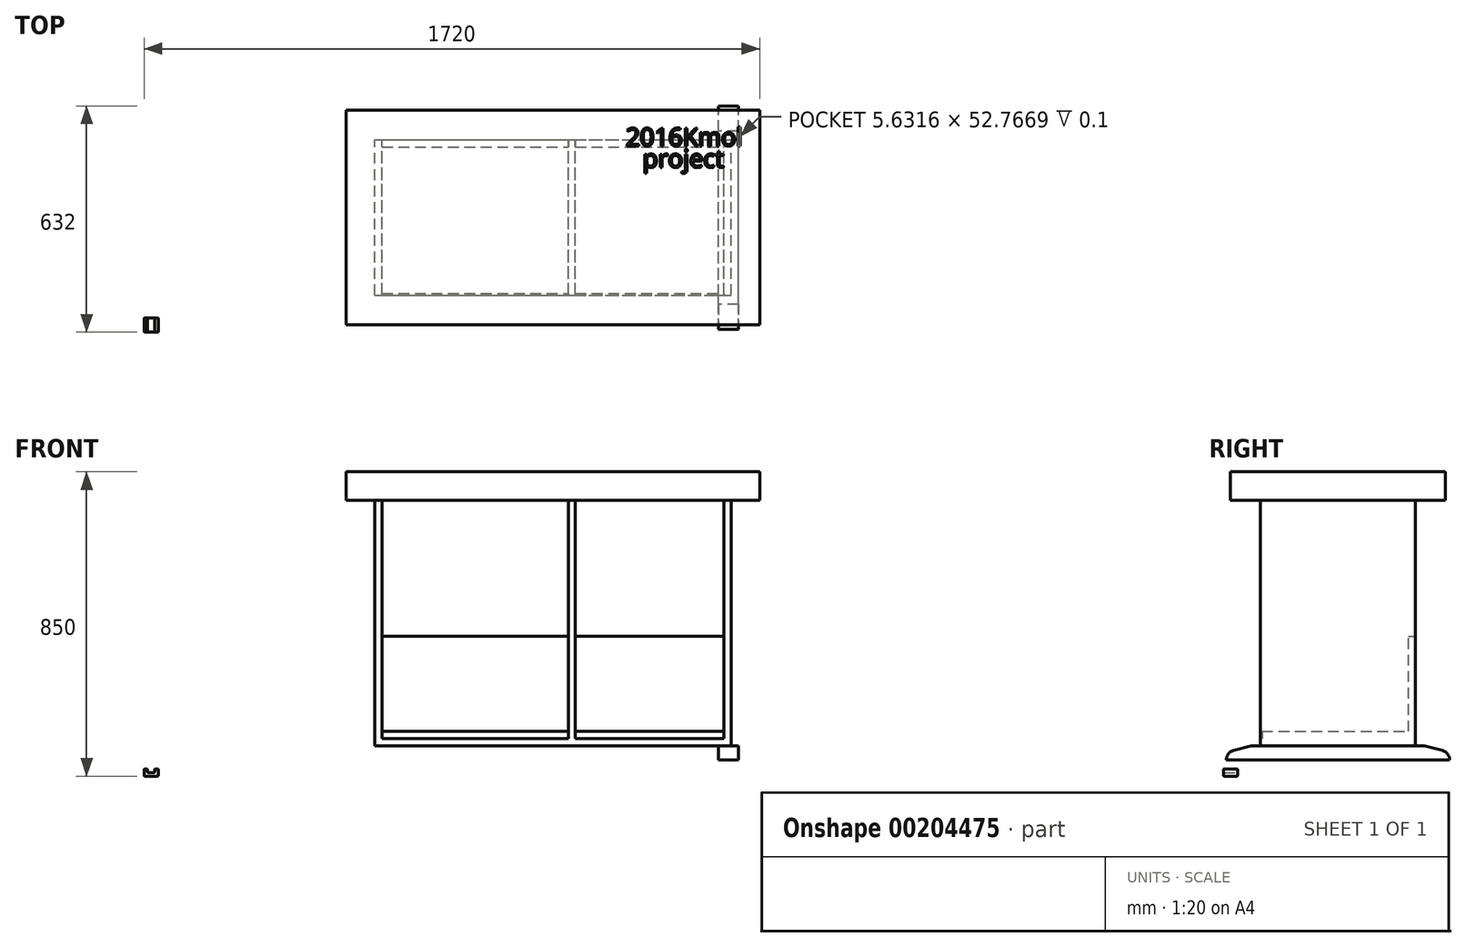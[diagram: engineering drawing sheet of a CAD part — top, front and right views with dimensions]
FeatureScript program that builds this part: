
annotation { "Feature Type Name" : "Feature", "Feature Type Description" : "" }
export const myFeature = defineFeature(function(context is Context, id is Id, definition is map)
    precondition{}
    {
        {
            var Q0;
            Q0=qCreatedBy(makeId("Top.planeOp"),FACE);
            cPlane(context, id + "F0", {"entities" : qUnion([Q0]), "cplaneType" : CPlaneType.OFFSET, "offset" : 770 * mm, "width" : 150 * mm, "height" : 150 * mm});
        }
        {
            var Q0;
            Q0=qCreatedBy(id+"F0.planeOp",FACE);
            var sketch = newSketch(context, id + "F1", { "sketchPlane" : qUnion([Q0])});
            skLineSegment(sketch, "E0.bottom", {"start": v(545, 0) * mm, "end": v(1700, 0) * mm});
            skLineSegment(sketch, "E0.top", {"start": v(545, 600) * mm, "end": v(1700, 600) * mm});
            skLineSegment(sketch, "E0.left", {"start": v(545, 0) * mm, "end": v(545, 600) * mm});
            skLineSegment(sketch, "E0.right", {"start": v(1700, 0) * mm, "end": v(1700, 600) * mm});
            skSolve(sketch);
        }
        {
            var Q0;
            Q0=makeQuery(id+"F1.imprint","IMPRINT",FACE,{"disambiguationData":[TD([[makeQuery(id+"F1.imprint","IMPRINT",EDGE,{"derivedFrom":sQuery(id+"F1.wireOp",EDGE,"E0.bottom")}),1.0]])]});
            extrude(context, id + "F2", {"entities" : qUnion([Q0]), "depth" : 80 * mm});
        }
        {
            var Q0;
            Q0=makeQuery(id+"F2.opExtrude","CAP_FACE",FACE,{"disambiguationData":[OSD([sQuery(id+"F1.wireOp",EDGE,"E0.bottom"),sQuery(id+"F1.wireOp",EDGE,"E0.top"),sQuery(id+"F1.wireOp",EDGE,"E0.left"),sQuery(id+"F1.wireOp",EDGE,"E0.right")])],"isStart":true});
            var sketch = newSketch(context, id + "F3", { "sketchPlane" : qUnion([Q0])});
            skLineSegment(sketch, "E1.bottom", {"start": v(1600, -83) * mm, "end": v(1620, -83) * mm});
            skLineSegment(sketch, "E1.top", {"start": v(1600, -517) * mm, "end": v(1620, -517) * mm});
            skLineSegment(sketch, "E1.left", {"start": v(1600, -83) * mm, "end": v(1600, -517) * mm});
            skLineSegment(sketch, "E1.right", {"start": v(1620, -83) * mm, "end": v(1620, -517) * mm});
            skLineSegment(sketch, "E2.bottom", {"start": v(1165, -83) * mm, "end": v(1185, -83) * mm});
            skLineSegment(sketch, "E2.top", {"start": v(1165, -517) * mm, "end": v(1185, -517) * mm});
            skLineSegment(sketch, "E2.left", {"start": v(1185, -83) * mm, "end": v(1185, -517) * mm});
            skLineSegment(sketch, "E2.right", {"start": v(1165, -83) * mm, "end": v(1165, -517) * mm});
            skLineSegment(sketch, "E3.bottom", {"start": v(625, -83) * mm, "end": v(645, -83) * mm});
            skLineSegment(sketch, "E3.top", {"start": v(625, -517) * mm, "end": v(645, -517) * mm});
            skLineSegment(sketch, "E3.left", {"start": v(625, -83) * mm, "end": v(625, -517) * mm});
            skLineSegment(sketch, "E3.right", {"start": v(645, -83) * mm, "end": v(645, -517) * mm});
            skSolve(sketch);
        }
        {
            var Q0;
            Q0=qSketchRegion(id+"F3",true);
            extrude(context, id + "F4", {"entities" : qUnion([Q0]), "operationType" : NewBodyOperationType.ADD, "depth" : 685 * mm});
        }
        {
            var Q0;
            Q0=makeQuery(id+"F4.opExtrude","CAP_FACE",FACE,{"disambiguationData":[OSD([sQuery(id+"F3.wireOp",EDGE,"E3.bottom"),sQuery(id+"F3.wireOp",EDGE,"E3.top"),sQuery(id+"F3.wireOp",EDGE,"E3.left"),sQuery(id+"F3.wireOp",EDGE,"E3.right")])],"isStart":false});
            var sketch = newSketch(context, id + "F5", { "sketchPlane" : qUnion([Q0])});
            skLineSegment(sketch, "E4.bottom", {"start": v(625, -517) * mm, "end": v(1620, -517) * mm});
            skLineSegment(sketch, "E4.top", {"start": v(625, -83) * mm, "end": v(1620, -83) * mm});
            skLineSegment(sketch, "E4.left", {"start": v(625, -517) * mm, "end": v(625, -83) * mm});
            skLineSegment(sketch, "E4.right", {"start": v(1620, -517) * mm, "end": v(1620, -83) * mm});
            skSolve(sketch);
        }
        {
            var Q0;
            {var subQ2=sQuery(id+"F5.wireOp",EDGE,"E4.right");Q0=makeQuery(id+"F5.imprint","IMPRINT",FACE,{"disambiguationData":[TD([[makeQuery(id+"F5.imprint","IMPRINT",EDGE,{"derivedFrom":subQ2}),1.0]])]});}
            extrude(context, id + "F6", {"entities" : qUnion([Q0]), "operationType" : NewBodyOperationType.ADD, "oppositeDirection" : true, "depth" : 40 * mm});
        }
        {
            var Q0;
            Q0=makeQuery(id+"F6.boolean.opBoolean","MERGE",FACE,{"derivedFrom":[makeQuery(id+"F4.opExtrude","SWEPT_FACE",FACE,{"disambiguationData":[OSD([sQuery(id+"F3.wireOp",EDGE,"E1.bottom")])]}),makeQuery(id+"F4.opExtrude","SWEPT_FACE",FACE,{"disambiguationData":[OSD([sQuery(id+"F3.wireOp",EDGE,"E2.bottom")])]}),makeQuery(id+"F4.opExtrude","SWEPT_FACE",FACE,{"disambiguationData":[OSD([sQuery(id+"F3.wireOp",EDGE,"E3.bottom")])]}),makeQuery(id+"F6.opExtrude","SWEPT_FACE",FACE,{"disambiguationData":[OSD([sQuery(id+"F5.wireOp",EDGE,"E4.top")])]})]});
            var sketch = newSketch(context, id + "F7", { "sketchPlane" : qUnion([Q0])});
            skLineSegment(sketch, "E5.bottom", {"start": v(645, 125) * mm, "end": v(1165, 125) * mm});
            skLineSegment(sketch, "E5.top", {"start": v(645, 105) * mm, "end": v(1165, 105) * mm});
            skLineSegment(sketch, "E5.left", {"start": v(645, 125) * mm, "end": v(645, 105) * mm});
            skLineSegment(sketch, "E5.right", {"start": v(1165, 125) * mm, "end": v(1165, 105) * mm});
            skLineSegment(sketch, "E6.bottom", {"start": v(1185, 125) * mm, "end": v(1600, 125) * mm});
            skLineSegment(sketch, "E6.top", {"start": v(1185, 105) * mm, "end": v(1600, 105) * mm});
            skLineSegment(sketch, "E6.left", {"start": v(1185, 125) * mm, "end": v(1185, 105) * mm});
            skLineSegment(sketch, "E6.right", {"start": v(1600, 125) * mm, "end": v(1600, 105) * mm});
            skSolve(sketch);
        }
        {
            var Q0;
            Q0=qSketchRegion(id+"F7",true);
            extrude(context, id + "F8", {"entities" : qUnion([Q0]), "operationType" : NewBodyOperationType.REMOVE, "oppositeDirection" : true, "depth" : 5 * mm});
        }
        {
            var Q0;
            Q0=makeQuery(id+"F8.boolean.opBoolean","MERGE",FACE,{"derivedFrom":[makeQuery(id+"F4.opExtrude","SWEPT_FACE",FACE,{"disambiguationData":[OSD([sQuery(id+"F3.wireOp",EDGE,"E1.left")])]}),makeQuery(id+"F8.opExtrude","SWEPT_FACE",FACE,{"disambiguationData":[OSD([sQuery(id+"F7.wireOp",EDGE,"E6.right")])]})]});
            var sketch = newSketch(context, id + "F9", { "sketchPlane" : qUnion([Q0])});
            skLineSegment(sketch, "E7.bottom", {"start": v(-517, 390) * mm, "end": v(-497, 390) * mm});
            skLineSegment(sketch, "E7.top", {"start": v(-517, 125) * mm, "end": v(-497, 125) * mm});
            skLineSegment(sketch, "E7.left", {"start": v(-517, 390) * mm, "end": v(-517, 125) * mm});
            skLineSegment(sketch, "E7.right", {"start": v(-497, 390) * mm, "end": v(-497, 125) * mm});
            skSolve(sketch);
        }
        {
            var Q0;
            Q0=qSketchRegion(id+"F9",true);
            var Q1;
            Q1=makeQuery(id+"F8.boolean.opBoolean","MERGE",FACE,{"derivedFrom":[makeQuery(id+"F4.opExtrude","SWEPT_FACE",FACE,{"disambiguationData":[OSD([sQuery(id+"F3.wireOp",EDGE,"E3.right")])]}),makeQuery(id+"F8.opExtrude","SWEPT_FACE",FACE,{"disambiguationData":[OSD([sQuery(id+"F7.wireOp",EDGE,"E5.left")])]})]});
            extrude(context, id + "F10", {"entities" : qUnion([Q0]), "operationType" : NewBodyOperationType.ADD, "endBound" : BoundingType.UP_TO_SURFACE, "endBoundEntityFace" : qUnion([Q1]), "depth" : 25 * mm});
        }
        {
            var Q0;
            Q0=makeQuery(id+"F2.opExtrude","CAP_FACE",FACE,{"disambiguationData":[OSD([sQuery(id+"F1.wireOp",EDGE,"E0.bottom"),sQuery(id+"F1.wireOp",EDGE,"E0.top"),sQuery(id+"F1.wireOp",EDGE,"E0.left"),sQuery(id+"F1.wireOp",EDGE,"E0.right")])],"isStart":false});
            var sketch = newSketch(context, id + "F11", { "sketchPlane" : qUnion([Q0])});
            skText(sketch, "E8", { "text": "2016Kmol", "fontName": "OpenSans-Regular.ttf"});
            skText(sketch, "E9", { "text": "project", "fontName": "OpenSans-Regular.ttf"});
            const initialGuessF11  = {"E8": [1.32592, 0.5, 1, 0, 0.05], "E9": [1.37295, 0.44, 1, 0, 0.05]};
            skSetInitialGuess(sketch, initialGuessF11);
            skSolve(sketch);
        }
        {
            var Q0;
            Q0=qSketchRegion(id+"F11",true);
            extrude(context, id + "F12", {"entities" : qUnion([Q0]), "operationType" : NewBodyOperationType.REMOVE, "oppositeDirection" : true, "depth" : 0.1 * mm});
        }
        {
            var Q0;
            Q0=makeQuery(id+"F4.opExtrude","SWEPT_FACE",FACE,{"disambiguationData":[OSD([sQuery(id+"F3.wireOp",EDGE,"E1.right")])]});
            var sketch = newSketch(context, id + "F13", { "sketchPlane" : qUnion([Q0])});
            skLineSegment(sketch, "E10", {"start": v(58, 85) * mm, "end": v(8, 71.24) * mm});
            skArc(sketch, "E11", {"start": v(8, 71.24) * mm, "mid": v(-6.43, 61.5) * mm, "end": v(-12, 45) * mm});
            skLineSegment(sketch, "E12", {"start": v(-12, 45) * mm, "end": v(300, 45) * mm});
            skPoint(sketch, "E12.endSnap0", {"position": v(300, 85) * mm});
            skLineSegment(sketch, "E13", {"start": v(58, 85) * mm, "end": v(300, 85) * mm});
            skLineSegment(sketch, "E14", {"start": v(300, 85) * mm, "end": v(300, -33.8) * mm, "construction": true});
            skLineSegment(sketch, "E15.MirrorCS", {"start": v(542, 85) * mm, "end": v(300, 85) * mm});
            skLineSegment(sketch, "E16.MirrorCS", {"start": v(612, 45) * mm, "end": v(300, 45) * mm});
            skLineSegment(sketch, "E17.MirrorCS", {"start": v(542, 85) * mm, "end": v(592, 71.24) * mm});
            skArc(sketch, "E18.MirrorCS", {"start": v(592, 71.24) * mm, "mid": v(606.43, 61.5) * mm, "end": v(612, 45) * mm});
            skSolve(sketch);
        }
        {
            var Q0;
            Q0=qSketchRegion(id+"F13",true);
            extrude(context, id + "F14", {"entities" : qUnion([Q0]), "operationType" : NewBodyOperationType.ADD, "depth" : 20 * mm, "hasSecondDirection" : true, "secondDirectionOppositeDirection" : true, "secondDirectionDepth" : 35 * mm});
        }
        {
            var Q0;
            Q0=qCreatedBy(makeId("Right.planeOp"),FACE);
            cPlane(context, id + "F15", {"entities" : qUnion([Q0]), "cplaneType" : CPlaneType.OFFSET, "offset" : 1122.5 * mm, "width" : 150 * mm, "height" : 150 * mm});
        }
        {
            var Q0;
            Q0=qCreatedBy(makeId("Front.planeOp"),FACE);
            var sketch = newSketch(context, id + "F16", { "sketchPlane" : qUnion([Q0])});
            skLineSegment(sketch, "E19", {"start": v(-20, 0) * mm, "end": v(20, 0) * mm});
            skLineSegment(sketch, "E20", {"start": v(20, 0) * mm, "end": v(20, 20) * mm});
            skLineSegment(sketch, "E21", {"start": v(20, 20) * mm, "end": v(10, 20) * mm});
            skLineSegment(sketch, "E22", {"start": v(10, 20) * mm, "end": v(10, 10) * mm});
            skLineSegment(sketch, "E23", {"start": v(10, 10) * mm, "end": v(-10, 10) * mm});
            skLineSegment(sketch, "E24", {"start": v(-10, 10) * mm, "end": v(-10, 20) * mm});
            skLineSegment(sketch, "E25", {"start": v(-10, 20) * mm, "end": v(-20, 20) * mm});
            skLineSegment(sketch, "E26", {"start": v(-20, 20) * mm, "end": v(-20, 0) * mm});
            skSolve(sketch);
        }
        {
            var Q0;
            Q0 = qSketchRegion(id + "F16", true);
            extrude(context, id + "F17", {"entities" : qUnion([Q0]), "depth" : 20 * mm, "offsetDistance" : 25 * mm, "hasSecondDirection" : true, "secondDirectionOppositeDirection" : true, "secondDirectionDepth" : 20 * mm});
        }
        {
            var Q0;
            Q0=makeQuery(id+"F17.opExtrude","CAP_FACE",FACE,{"disambiguationData":[OSD([sQuery(id+"F16.wireOp",EDGE,"E19"),sQuery(id+"F16.wireOp",EDGE,"E20"),sQuery(id+"F16.wireOp",EDGE,"E21"),sQuery(id+"F16.wireOp",EDGE,"E22"),sQuery(id+"F16.wireOp",EDGE,"E23"),sQuery(id+"F16.wireOp",EDGE,"E24"),sQuery(id+"F16.wireOp",EDGE,"E25"),sQuery(id+"F16.wireOp",EDGE,"E26")])],"isStart":false});
            var Q1;
            Q1=makeQuery(id+"F17.opExtrude","SWEPT_FACE",FACE,{"disambiguationData":[OSD([sQuery(id+"F16.wireOp",EDGE,"E26")])]});
            var Q2;
            Q2=makeQuery(id+"F17.opExtrude","SWEPT_FACE",FACE,{"disambiguationData":[OSD([sQuery(id+"F16.wireOp",EDGE,"E19")])]});
            var Q3;
            Q3=makeQuery(id+"F17.opExtrude","CAP_FACE",FACE,{"disambiguationData":[OSD([sQuery(id+"F16.wireOp",EDGE,"E19"),sQuery(id+"F16.wireOp",EDGE,"E20"),sQuery(id+"F16.wireOp",EDGE,"E21"),sQuery(id+"F16.wireOp",EDGE,"E22"),sQuery(id+"F16.wireOp",EDGE,"E23"),sQuery(id+"F16.wireOp",EDGE,"E24"),sQuery(id+"F16.wireOp",EDGE,"E25"),sQuery(id+"F16.wireOp",EDGE,"E26")])],"isStart":true});
            var Q4;
            Q4=makeQuery(id+"F17.opExtrude","SWEPT_FACE",FACE,{"disambiguationData":[OSD([sQuery(id+"F16.wireOp",EDGE,"E20")])]});
            var Q5;
            Q5=makeQuery(id+"F17.opExtrude","SWEPT_FACE",FACE,{"disambiguationData":[OSD([sQuery(id+"F16.wireOp",EDGE,"E21")])]});
            var Q6;
            Q6=makeQuery(id+"F17.opExtrude","SWEPT_FACE",FACE,{"disambiguationData":[OSD([sQuery(id+"F16.wireOp",EDGE,"E23")])]});
            var Q7;
            Q7=makeQuery(id+"F17.opExtrude","SWEPT_FACE",FACE,{"disambiguationData":[OSD([sQuery(id+"F16.wireOp",EDGE,"E25")])]});
            fillet(context, id + "F18", {"entities" : qUnion([Q0, Q1, Q2, Q3, Q4, Q5, Q6, Q7]), "radius" : 2 * mm, "tangentPropagation" : true, "allowEdgeOverflow" : false});
        }
    });
